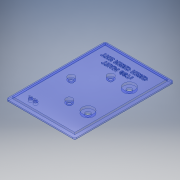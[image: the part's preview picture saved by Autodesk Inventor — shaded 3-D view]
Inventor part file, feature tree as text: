
AUTODESK INVENTOR PART (.ipt)
format: ipt  version: 2017 SP1 (Build 210196100, 196)  size: 518,656 bytes
history: native  units: in
note: dims shown in document units (in); Inventor stores cm internally (conversion verified against a paired STEP export)
features: sketch x7, extrude x4, hole x3, projected_geometry x3, chamfer x1, fillet x1
ambient origin geometry x8: Origin, YZ Plane, XZ Plane, XY Plane, X Axis, Y Axis, Z Axis, Center Point
bodies: Solid1 (feature_tree)
feature tree (19):
  extrude  "Extrusion1"  Depth=4.2in
  extrude  "Extrusion2"  Depth=0.2in
  chamfer  "Chamfer1"  Distance=0.125in
  fillet  "Fillet1"  Radius=0.125in
  hole  "Hole3"  [1 undecoded]
  hole  "Hole4"  [1 undecoded]
  extrude  "Extrusion4"  Depth=2.28in
  hole  "Hole5"  [1 undecoded]
  extrude  "Extrusion5"  Depth=1.14in
  sketch  "Sketch1"  dims[d0=6.05in d1=4.2in]
  sketch  "Sketch2"  dims[d2=0.125in d3=0.0in d4=0.2in d5=0.125in d6=0.0in]
  projected_geometry  "Projected Loop1"
  sketch  "Sketch6"  dims[d35=0.05in d36=0.125in d37=45.0deg d38=0.125in]
  projected_geometry  "Projected Loop4"
  sketch  "Sketch7"  dims[d39=1.5616in d40=1.5616in]
  sketch  "Sketch8"  dims[d41=2.5267in d42=0.76in]
  sketch  "Sketch9"  dims[d43=0.76in d44=2.28in]
  projected_geometry  "Projected Loop5"
  sketch  "Sketch10"  dims[d45=1.14in d46=1.14in d47=0.25in d48=0.75in d49=0.4in d50=0.1625in d51=0.5635in d52=1.0in d53=0.8108in d54=1.14in d55=1.14in d56=0.3in d57=0.75in d58=0.7in d59=0.15in d60=0.5635in d61=1.0in d62=0.8108in d63=0.23in d64=0.3in d65=0.75in d66=0.75in d67=0.125in d68=0.0in d69=0.0625in d70=0.0625in d71=0.0625in d72=0.0625in d73=0.125in d74=0.08in d75=0.75in d76=1.0in d77=0.15in d78=0.5635in d79=1.0in d80=0.8108in d81=1.0in d82=3.0in d83=0.15in d84=0.15in d85=0.05in d86=0.0in]
note: 3 required parameter values undecoded (feature->parameter linkage not recoverable at this tier; creation-order binding heuristic only, values carry confidence <= 0.55)
